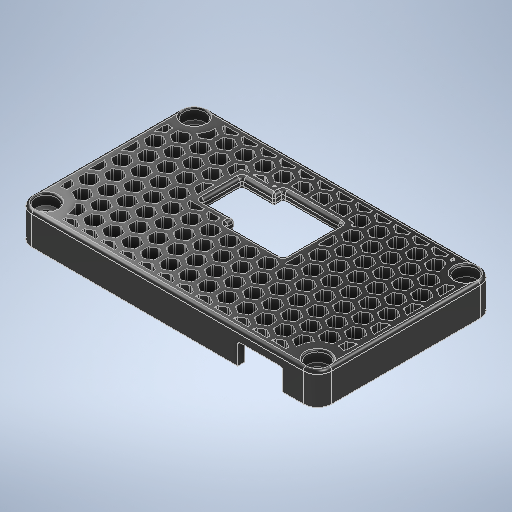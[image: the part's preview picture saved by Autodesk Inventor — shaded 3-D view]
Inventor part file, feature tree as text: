
AUTODESK INVENTOR PART (.ipt)
format: ipt  version: 2025 (Build 290162000, 162)  size: 3,558,400 bytes
history: native  units: mm
features: reference x16, sketch x8, extrude x8, other x5, fillet x4, thicken_offset x4, chamfer x2, projected_geometry x2
ambient origin geometry x8: Origin, YZ Plane, XZ Plane, XY Plane, X Axis, Y Axis, Z Axis, Center Point
bodies: Solid1 (feature_tree)
feature tree (49):
  sketch  "Sketch1"  dims[d0=2.0mm d1=80.0mm]
  extrude  "Extrusion1"  Depth=80.0mm
  extrude  "Extrusion2"  Depth=1.0mm TaperAngle=0.0deg
  extrude  "Extrusion3"  Depth=45.5mm
  fillet  "Fillet2"  Radius=3.2mm
  fillet  "Fillet3"  Radius=6.0mm
  extrude  "Extrusion4"  Depth=1.0mm
  thicken_offset  "Thicken1"
  thicken_offset  "Thicken2"
  thicken_offset  "Thicken3"
  thicken_offset  "Thicken4"
  chamfer  "Chamfer2"  Distance=0.5mm
  chamfer  "Chamfer3"  Distance=1.0mm
  fillet  "Fillet5"  Radius=0.5mm
  extrude  "Extrusion5"  Depth=0.5mm
  fillet  "Fillet6"  Radius=0.5mm
  sketch  "Sketch4"  dims[d14=3.0mm d15=0.0mm d16=1.0mm]
  extrude  "Extrusion7"  Depth=0.5mm
  extrude  "Extrusion8"  Depth=0.5mm TaperAngle=45.0deg
  sketch  "Sketch5"  dims[d22=0.5mm]
  extrude  "Extrusion9"  Depth=0.5mm TaperAngle=45.0deg
  sketch  "Sketch3"  dims[d3=2.0mm d4=1.0mm d5=0.0mm]
  reference  "Reference1"
  reference  "Reference2"
  reference  "Reference3"
  reference  "Reference4"
  reference  "Reference5"
  reference  "Reference6"
  reference  "Reference7"
  projected_geometry  "Projected Loop1"
  projected_geometry  "Projected Loop2"
  sketch  "Sketch Rectangular Pattern3"  dims[d6=6.0mm d7=0.0mm d10=45.5mm d11=3.2mm d13=6.0mm]
  sketch  "Sketch Rectangular Pattern4"  dims[d17=0.5mm]
  sketch  "Sketch Rectangular Pattern5"  dims[d23=0.5mm]
  reference  "Reference8"
  reference  "Reference9"
  reference  "Reference10"
  reference  "Reference11"
  reference  "Reference12"
  reference  "Reference13"
  reference  "Reference14"
  reference  "Reference15"
  reference  "Reference16"
  sketch  "Sketch6"  dims[d24=0.5mm d25=0.5mm d26=1.0mm d27=0.0mm d28=0.5mm d29=0.5mm d30=0.5mm d31=0.5mm d32=2.0mm d33=2.0mm d34=45.0deg d35=1.0mm d36=2.0mm d37=45.0deg d38=1.0mm d39=1.0mm d40=1.0mm d41=2.0mm d42=0.0mm d43=0.0mm d44=0.5mm d46=1.0mm d47=4.0mm d51=0.5mm d53=4.0mm d54=0.5mm d74=60.0mm d76=5.333333mm d77=10.0mm d79=5.333333mm d81=60.0mm d83=5.333333mm d84=10.0mm d86=10.0mm d88=170.0mm d90=5.333333mm d91=10.0mm d93=10.0mm d95=0.0mm d96=0.0mm d100=10.0mm d101=0.0mm d102=12.5mm d103=6.5mm d104=0.5mm d105=2.0mm d106=0.0mm d18=0.5mm d19=0.872665mm d20=0.5mm d21=0.872665mm d97=0.0mm d98=0.0mm d99=0.0mm]
  parser-record x1  (decoder bookkeeping rows leaked as tree rows — omitted from the tree; the rows remain in map.json)
  other  "RemoteCameraModule.iam"
  other  "HEATSINK14x14:1"
  other  "HEATSINK9x9:1"
  other  "OPiZ2W_:1"
note: 1 file-system path scrubbed to <path> (originals preserved in map.json)
